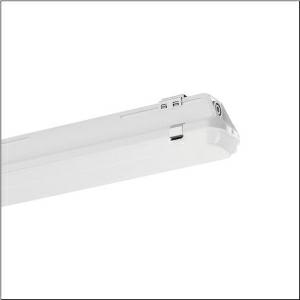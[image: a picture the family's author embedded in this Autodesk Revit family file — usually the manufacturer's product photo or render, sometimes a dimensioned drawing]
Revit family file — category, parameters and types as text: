
# Revit family: monsun_r__11_51fp22mp4b0u_feed
name_source: partatom
category: Lighting Fixtures
units: mm (PartAtom-declared; Revit-internal decimal feet)

## family parameters
Cut with Voids When Loaded = No
Host = Face
Light Source = No
Part Type = Normal
Room Calculation Point = No
Round Connector Dimension = Use Diameter
Shared = No

## types (1)
- --- (1 x LED, 10520 lm, 62.4 W, 4000K)
    Apparent Load = 62 VA
    CIE Flux Codes = 49 78 94 96 100
    Color Rendering = 80
    Color Temperature = 4000K
    Default Elevation = 1800 mm
    Description = Monsun® 11, damp-proof luminaire, chain hanger, primary light control with lens, primary optical cover: enclosure, of PC, light emission: direct distribution, primary light characteristic: symmetric, installation type: suspended mounting, surface-mounted, horizontal mounting, vertical mounting, LED, rated luminous flux: 10.520lm, luminous efficacy: 167lm/W, light colour: 840, colour temperature: 4000K, control gear: ON/OFF Multilumen, with terminal, 3-pole, max. 2.5mm², mains connection: 220..240V, AC, 50/60Hz, rated input power: 62W, luminaire housing, of glass-fibre reinforced polyester, uncoated, bright grey, incl. chain hanger, length: 1.590mm, width: 90mm, height: 88mm, clip for enclosure, of stainless steel (V2A), ceiling mounting element, of stainless steel (V2A), chain hanger, of stainless steel (V2A), protection rating (complete): IP66, insulation class (complete): insulation class I (protective earthing), certification: CE, ENEC, VDE, UKCA, protection symbol: D, impact resistance: IK08, permissible operating ambient temperature: -35..+35°C, standard: EN 50419, EN 60598-2-1, contact your sales advisor before using the luminaires in applications with unclear chemical exposure, large temperature fluctuations or condensation-forming humidity, LABS conformity tested according to VDMA 24364:2018-05, no direct snow, no direct sun, no direct rain, for indoor or canopied outdoor use, corresponds to IFS (International Featured Standards) requirements for safety and quality in the food industry, packaging unit: 1 piece
    Height = 89 mm
    Lamp = 1 x LED
    Lamp Light Flux = 10520 lm
    Lamp Power = 62.4 W
    Lamp count = 1
    Length = 1590 mm
    Luminous efficacy = 169 lm/W
    Manufacturer = Siteco
    ModVariant = No
    Model = 51FP22MP4B0U
    Mounting Place = Ceiling
    Mounting Type = Surface mounted
    Number of Poles = 1
    OnlyDefault = Yes
    Power Factor = 1
    Product Name = Monsun® 11
    Product group = damp-proof luminaire
    ProductGroupID = 300
    Protection Class = Protection class I
    Protection Degree = IP 66
    RLX_Detail_Level = 1
    RLX_Emergency_Light_Flux = 0 lm
    RLX_Emergency_Type = 0
    RLX_Emergency_Type_DB = No
    RlxData = <blob elided: 90117 chars, md5=758f20e5>
    Socket = socket
    Standby Power = 0 W
    System Light Flux = 10520 lm
    System Power = 62 W
    Type Comments = factory setting: luminous flux: 100 % | (A | C | E) | 147 mA
    Type Image = l_1349237.jpg
    URL = http://relux.com
    VarID = @adj_018628
    Voltage = 0 V
    Weight = 0.00 kg
    Width = 90 mm

## geometry (parser evidence)
native form markers: Blend x4, Sweep x11
no freeform markers — native parametric forms only
